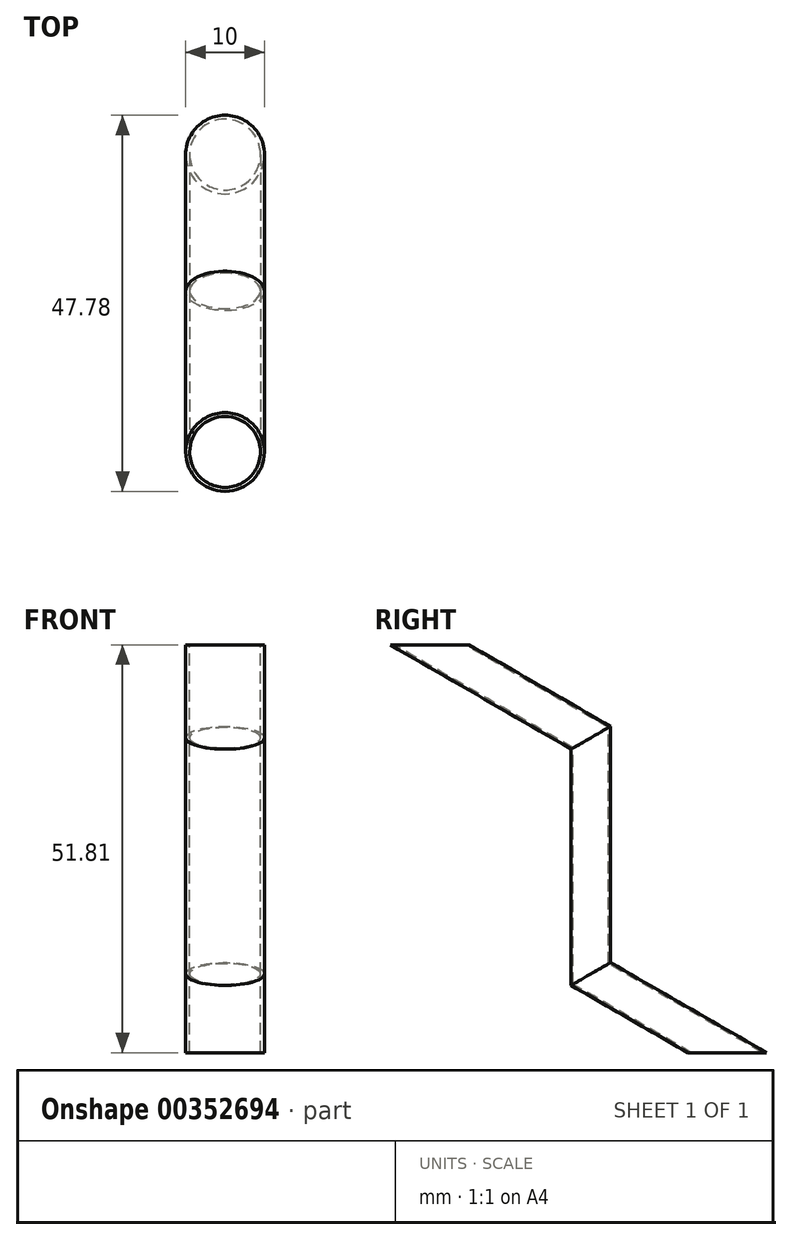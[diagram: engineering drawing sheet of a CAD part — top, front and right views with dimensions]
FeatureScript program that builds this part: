
annotation { "Feature Type Name" : "Feature", "Feature Type Description" : "" }
export const myFeature = defineFeature(function(context is Context, id is Id, definition is map)
    precondition{}
    {
        {
            var Q0;
            Q0=qCreatedBy(makeId("Top.planeOp"),FACE);
            var sketch = newSketch(context, id + "F0", { "sketchPlane" : qUnion([Q0])});
            skCircle(sketch, "E0", {"center": v(0, 0) * mm, "radius": 5 * mm});
            skCircle(sketch, "E1", {"center": v(0, 0) * mm, "radius": 4.5 * mm});
            skSolve(sketch);
        }
        {
            var Q0;
            Q0=qCreatedBy(makeId("Right.planeOp"),FACE);
            var sketch = newSketch(context, id + "F1", { "sketchPlane" : qUnion([Q0])});
            skLineSegment(sketch, "E2", {"start": v(0, 0) * mm, "end": v(-17.32, 10) * mm});
            skLineSegment(sketch, "E3", {"start": v(-17.32, 10) * mm, "end": v(-17.32, 40) * mm});
            skLineSegment(sketch, "E4", {"start": v(-17.32, 40) * mm, "end": v(-37.78, 51.81) * mm});
            skSolve(sketch);
        }
        {
            var Q0;
            Q0 = qSketchRegion(id + "F0", true);
            var Q1;
            Q1=sQuery(id+"F1.wireOp",EDGE,"E2");
            var Q2;
            Q2=sQuery(id+"F1.wireOp",EDGE,"E3");
            var Q3;
            Q3=sQuery(id+"F1.wireOp",EDGE,"E4");
            sweep(context, id + "F2", {"profiles" : qUnion([Q0]), "path" : qUnion([Q1, Q2, Q3])});
        }
    });
